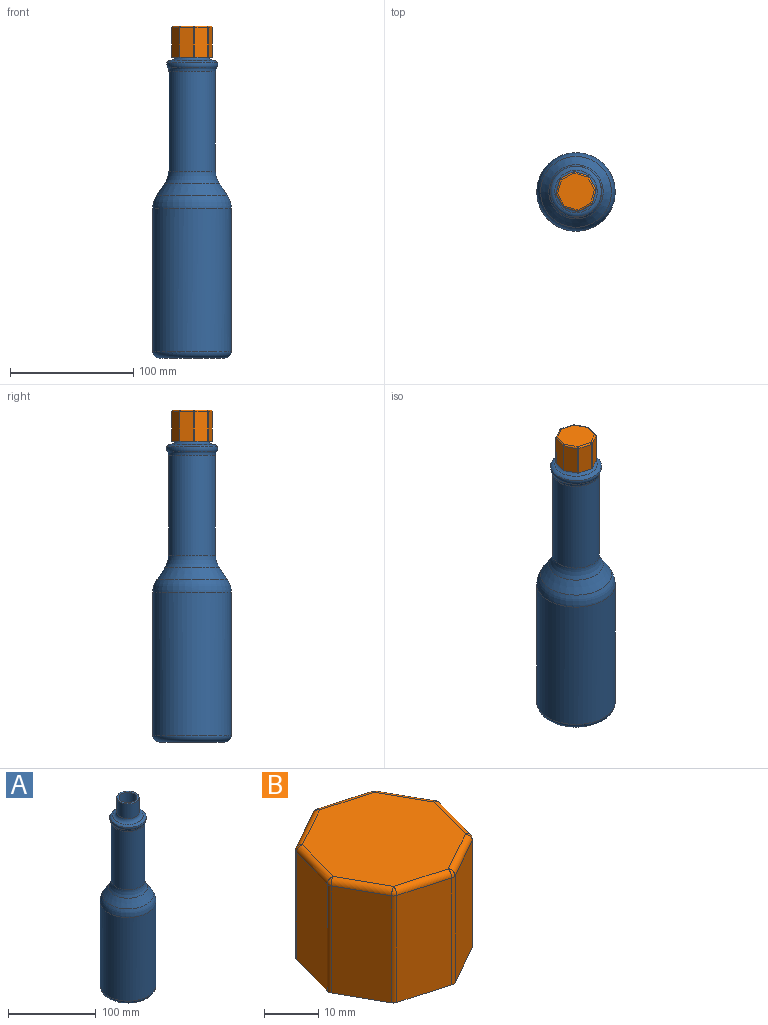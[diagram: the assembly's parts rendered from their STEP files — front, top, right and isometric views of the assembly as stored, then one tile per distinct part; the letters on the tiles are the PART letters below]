
ASSEMBLY  parts=2 mates=1
PART A: 25 faces, bbox 68.7x68.7x266.7 mm
  f0: cylinder r=31.75mm len=116.54mm, axis (0,0,-1), area 23248mm2, adj f2,f6
  f1: plane 53.34x53.34mm, normal (0,0,-1), area 2234.6mm2, adj f2
  f2: torus R=26.67mm, axis (0,0,1), area 1499.3mm2, adj f0,f1
  f3: cone r=31.75mm half-angle=33.7deg, axis (0,0,-1), area 1935.6mm2, adj f5,f6
  f4: cylinder r=19.05mm len=81.08mm, axis (0,0,-1), area 9704.3mm2, adj f5,f10
  f5: torus R=36.83mm, axis (0,0,1), area 1317.5mm2, adj f3,f4
  f6: torus R=13.97mm, axis (0,0,-1), area 2019.5mm2, adj f0,f3
  f7: cylinder r=12.7mm len=25.4mm, axis (0,0,-1), area 1626.3mm2, adj f8,f12
  f8: plane 25.4x25.4mm, normal (0,0,1), area 182.4mm2, adj f7,f20
  f9: torus R=16.67mm, axis (0,0,1), area 465.3mm2, adj f11,f12
  f10: torus R=24.13mm, axis (0,0,1), area 362.4mm2, adj f4,f11
  f11: torus R=15.67mm, axis (0,0,-1), area 559.2mm2, adj f9,f10
  f12: torus R=17.78mm, axis (0,0,1), area 668.2mm2, adj f7,f9
  f13: cylinder r=29.21mm len=116.54mm, axis (0,0,-1), area 21388.2mm2, adj f15,f19
  f14: plane 53.34x53.34mm, normal (0,0,1), area 2234.6mm2, adj f15
  f15: torus R=26.67mm, axis (0,0,1), area 709.1mm2, adj f13,f14
  f16: cone r=29.64mm half-angle=33.7deg, axis (0,0,-1), area 1774.6mm2, adj f18,f19
  f17: cylinder r=16.51mm len=81.08mm, axis (0,0,-1), area 8410.4mm2, adj f18,f22
  f18: torus R=36.83mm, axis (0,0,1), area 1325.9mm2, adj f16,f17
  f19: torus R=13.97mm, axis (0,0,-1), area 1596.1mm2, adj f13,f16
  f20: cylinder r=10.16mm len=20.38mm, axis (0,0,-1), area 1301mm2, adj f8,f24
  f21: torus R=16.67mm, axis (0,0,1), area 152.1mm2, adj f23,f24
  f22: torus R=24.13mm, axis (0,0,1), area 476.2mm2, adj f17,f23
  f23: torus R=15.67mm, axis (0,0,-1), area 181.2mm2, adj f21,f22
  f24: torus R=17.78mm, axis (0,0,1), area 881.4mm2, adj f20,f21
PART B: 43 faces, bbox 32.6x32.6x25.4 mm
  f0: plane 32.58x32.58mm, normal (0,0,-1), area 234.9mm2, adj f1,f2,f3,f4,f5,f6,f7,f8
  f1: plane 24.13x10.11mm, normal (-0.49,0.87,0), area 279.3mm2, adj f0,f24,f30,f33
  f2: plane 24.13x11.13mm, normal (-0.96,0.27,0), area 279.3mm2, adj f0,f27,f31,f33
  f3: plane 24.13x10.11mm, normal (-0.87,-0.49,0), area 279.3mm2, adj f0,f21,f26,f27
  f4: plane 24.13x11.13mm, normal (-0.27,-0.96,0), area 279.3mm2, adj f0,f15,f20,f21
  f5: plane 24.13x10.11mm, normal (0.49,-0.87,0), area 279.3mm2, adj f0,f10,f14,f15
  f6: plane 24.13x11.13mm, normal (0.96,-0.27,0), area 279.3mm2, adj f0,f10,f12,f13
  f7: plane 24.13x10.11mm, normal (0.87,0.49,0), area 279.3mm2, adj f0,f12,f18,f19
  f8: plane 24.13x11.13mm, normal (0.27,0.96,0), area 279.3mm2, adj f0,f18,f24,f25
  f9: plane 30.04x30.04mm, normal (0,0,1), area 646.7mm2, adj f13,f14,f19,f20,f25,f26,f30,f31
  f10: cylinder r=1.27mm len=24.13mm, axis (0,0,-1), area 24.1mm2, adj f0,f5,f6,f11
  f11: sphere r=1.27mm, area 1.3mm2, adj f10,f13,f14
  f12: cylinder r=1.27mm len=24.13mm, axis (0,0,-1), area 24.1mm2, adj f0,f6,f7,f16
  f13: cylinder r=1.27mm len=11.48mm, axis (-0.27,-0.96,0), area 23.1mm2, adj f6,f9,f11,f16
  f14: cylinder r=1.27mm len=10.73mm, axis (-0.87,-0.49,0), area 23.1mm2, adj f5,f9,f11,f17
  f15: cylinder r=1.27mm len=24.13mm, axis (0,0,-1), area 24.1mm2, adj f0,f4,f5,f17
  f16: sphere r=1.27mm, area 1.3mm2, adj f12,f13,f19
  f17: sphere r=1.27mm, area 1.3mm2, adj f14,f15,f20
  f18: cylinder r=1.27mm len=24.13mm, axis (0,0,-1), area 24.1mm2, adj f0,f7,f8,f22
  f19: cylinder r=1.27mm len=10.73mm, axis (0.49,-0.87,0), area 23.1mm2, adj f7,f9,f16,f22
  f20: cylinder r=1.27mm len=11.48mm, axis (-0.96,0.27,0), area 23.1mm2, adj f4,f9,f17,f23
  f21: cylinder r=1.27mm len=24.13mm, axis (0,0,-1), area 24.1mm2, adj f0,f3,f4,f23
  f22: sphere r=1.27mm, area 1.3mm2, adj f18,f19,f25
  f23: sphere r=1.27mm, area 1.3mm2, adj f20,f21,f26
  f24: cylinder r=1.27mm len=24.13mm, axis (0,0,-1), area 24.1mm2, adj f0,f1,f8,f28
  f25: cylinder r=1.27mm len=11.48mm, axis (0.96,-0.27,0), area 23.1mm2, adj f8,f9,f22,f28
  f26: cylinder r=1.27mm len=10.73mm, axis (-0.49,0.87,0), area 23.1mm2, adj f3,f9,f23,f29
  f27: cylinder r=1.27mm len=24.13mm, axis (0,0,-1), area 24.1mm2, adj f0,f2,f3,f29
  f28: sphere r=1.27mm, area 1.3mm2, adj f24,f25,f30
  f29: sphere r=1.27mm, area 1.3mm2, adj f26,f27,f31
  f30: cylinder r=1.27mm len=10.73mm, axis (0.87,0.49,0), area 23.1mm2, adj f1,f9,f28,f32
  f31: cylinder r=1.27mm len=11.48mm, axis (0.27,0.96,0), area 23.1mm2, adj f2,f9,f29,f32
  f32: sphere r=1.27mm, area 1.3mm2, adj f30,f31,f33
  f33: cylinder r=1.27mm len=24.13mm, axis (0,0,-1), area 24.1mm2, adj f0,f1,f2,f32
  f34: plane 22.86x9.19mm, normal (0.49,-0.87,0), area 240.5mm2, adj f0,f35,f41,f42
  f35: plane 22.86x10.12mm, normal (0.96,-0.27,0), area 240.5mm2, adj f0,f34,f36,f42
  f36: plane 22.86x9.19mm, normal (0.87,0.49,0), area 240.5mm2, adj f0,f35,f37,f42
  f37: plane 22.86x10.12mm, normal (0.27,0.96,0), area 240.5mm2, adj f0,f36,f38,f42
  f38: plane 22.86x9.19mm, normal (-0.49,0.87,0), area 240.5mm2, adj f0,f37,f39,f42
  f39: plane 22.86x10.12mm, normal (-0.96,0.27,0), area 240.5mm2, adj f0,f38,f40,f42
  f40: plane 22.86x9.19mm, normal (-0.87,-0.49,0), area 240.5mm2, adj f0,f39,f41,f42
  f41: plane 22.86x10.12mm, normal (-0.27,-0.96,0), area 240.5mm2, adj f0,f34,f40,f42
  f42: plane 27.31x27.31mm, normal (0,0,-1), area 534.5mm2, adj f34,f35,f36,f37,f38,f39,f40,f41
PLACE A t=(-115.13,7.16,-22.9)mm
PLACE B t=(-115.13,7.16,220.94)mm
MATE cylindrical B.f42 <-> A.f7  axis (0,0,-1) through (-115.13,7.16,243.8)mm
